# Revit family: Urinal-Hybrid-Sloan-HYB-7000_Series
name_source: partatom
category: Plumbing Fixtures
revit_build: Autodesk Revit 2014 (Build: 20130308_1515(x64)
units: mm (PartAtom-declared; Revit-internal decimal feet)

## types (1)
- HYB-7000
    ADA Compliant = Yes
    Assembly Code = D2010210
    CW Connection = No
    CWFU = 0
    Default Elevation = 24"
    Description = Complete Vitreous China Hybrid Urinal
    Fixture Color = White
    Flush Choice = Hybrid
    Flush Volume(s)/Flow Rate(s) = Waterfree
    HW Connection = No
    HWFU = 0
    High Efficiency = Yes
    Manufacturer = Sloan
    Material = Vitreous China-Sloan-White
    Model = HYB-7000
    Mounting = Wall Hung
    Order Code = 1007020
    Price = Prices may vary. Please consult Sloan Rep for most up-to-date price list.
    Product Documentation Link = https://specifications.sloan.com
    Product Page URL = https://www.sloan.com
    Revised Date = 2/3/2017
    Spud Location = Not Applicable
    URL = www.sloan.com
    Vent Connection = No
    WFU = 0
    Warranty = 3 Year (Limited)
    Waste Connection = Yes

## geometry (parser evidence)
native form markers: Sweep x2
no freeform markers — native parametric forms only
